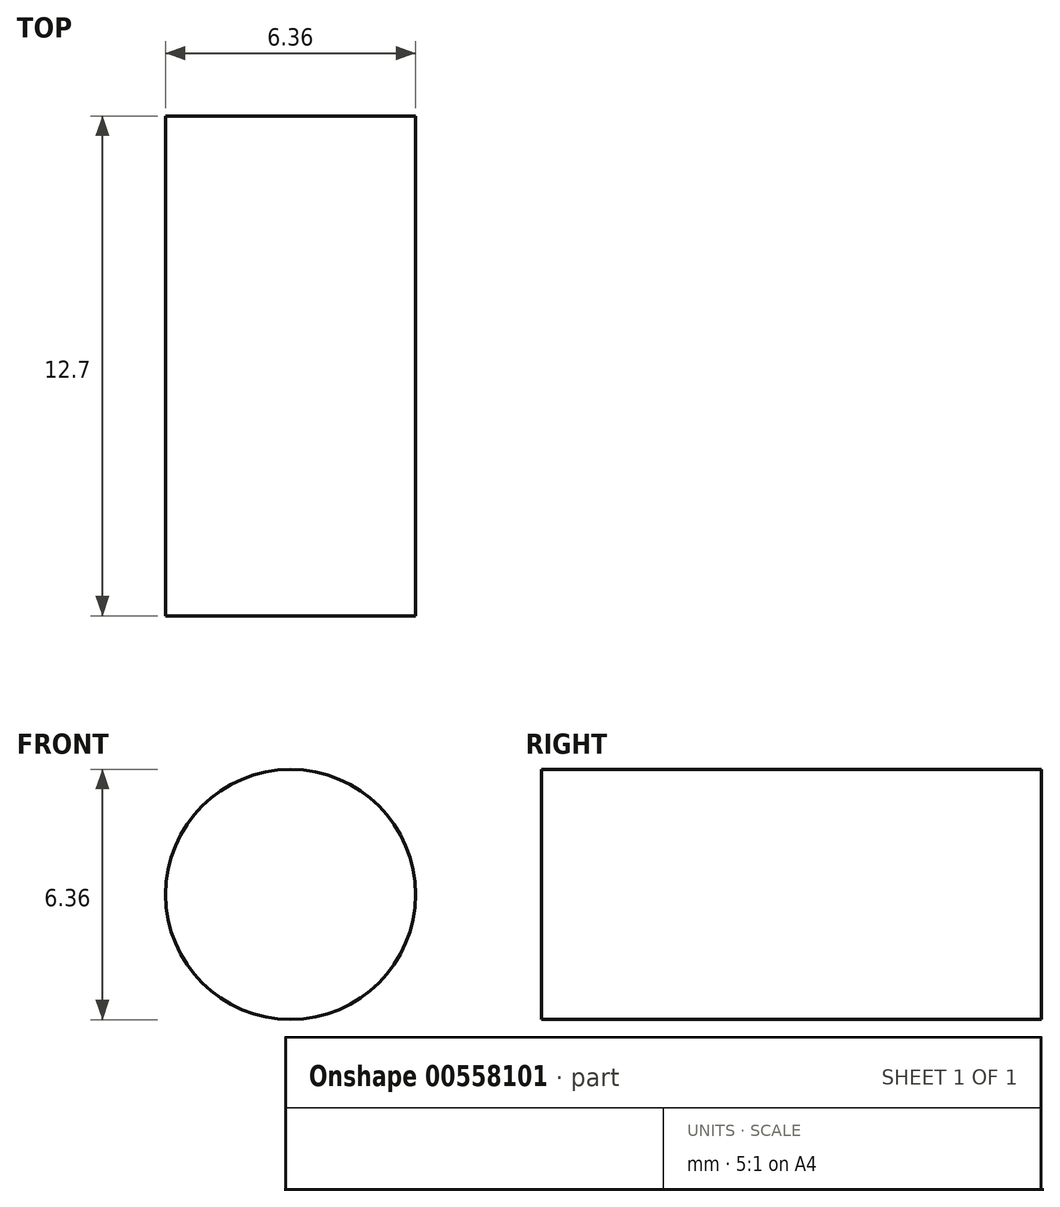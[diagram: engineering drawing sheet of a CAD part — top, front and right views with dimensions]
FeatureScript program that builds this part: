
annotation { "Feature Type Name" : "Feature", "Feature Type Description" : "" }
export const myFeature = defineFeature(function(context is Context, id is Id, definition is map)
    precondition{}
    {
        {
            var Q0;
            Q0=qCreatedBy(makeId("Front.planeOp"),FACE);
            var sketch = newSketch(context, id + "F0", { "sketchPlane" : qUnion([Q0])});
            skCircle(sketch, "E0", {"center": v(0, 0) * mm, "radius": 3.18 * mm});
            skSolve(sketch);
        }
        {
            var Q0;
            Q0 = qSketchRegion(id + "F0", true);
            extrude(context, id + "F1", {"entities" : qUnion([Q0]), "depth" : 12.7 * mm, "offsetDistance" : 25.4 * mm});
        }
    });
